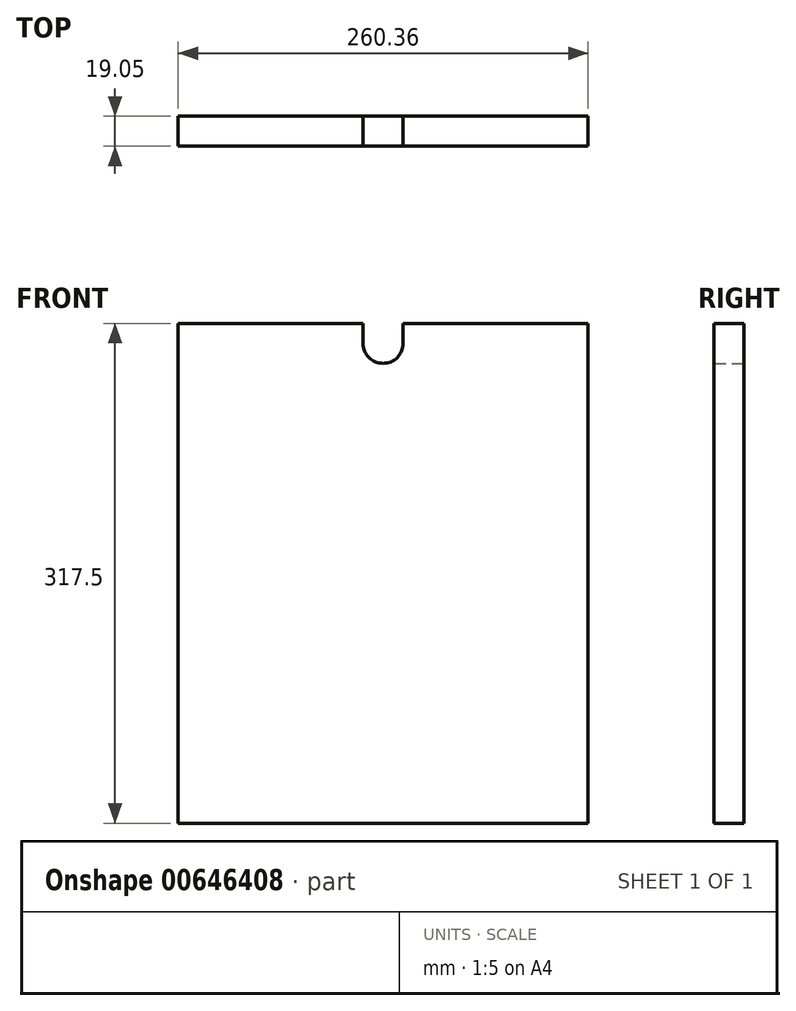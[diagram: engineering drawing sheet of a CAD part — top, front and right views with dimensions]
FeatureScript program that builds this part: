
annotation { "Feature Type Name" : "Feature", "Feature Type Description" : "" }
export const myFeature = defineFeature(function(context is Context, id is Id, definition is map)
    precondition{}
    {
        {
            var Q0;
            Q0=qCreatedBy(makeId("Front.planeOp"),FACE);
            var sketch = newSketch(context, id + "F0", { "sketchPlane" : qUnion([Q0])});
            skLineSegment(sketch, "E0.bottom", {"start": v(-130.18, 158.75) * mm, "end": v(130.18, 158.75) * mm});
            skLineSegment(sketch, "E0.top", {"start": v(-130.18, -158.75) * mm, "end": v(130.17, -158.75) * mm});
            skLineSegment(sketch, "E0.left", {"start": v(-130.17, 158.75) * mm, "end": v(-130.18, -158.75) * mm});
            skLineSegment(sketch, "E0.right", {"start": v(130.18, 158.75) * mm, "end": v(130.17, -158.75) * mm});
            skPoint(sketch, "E0.middle", {"position": v(0, 0) * mm});
            skLineSegment(sketch, "E1", {"start": v(0, 158.75) * mm, "end": v(0, 133.35) * mm});
            skPoint(sketch, "E1.endSnap0", {"position": v(0, 158.75) * mm});
            skCircle(sketch, "E2", {"center": v(0, 146.05) * mm, "radius": 12.7 * mm});
            skLineSegment(sketch, "E3", {"start": v(-12.7, 146.05) * mm, "end": v(-12.7, 158.75) * mm});
            skLineSegment(sketch, "E4", {"start": v(12.7, 146.05) * mm, "end": v(12.7, 158.75) * mm});
            skSolve(sketch);
        }
        {
            var Q0;
            Q0=makeQuery(id+"F0.imprint","IMPRINT",FACE,{"disambiguationData":[TD([[makeQuery(id+"F0.imprint","IMPRINT",EDGE,{"derivedFrom":sQuery(id+"F0.wireOp",EDGE,"E0.top")}),1.0]])]});
            extrude(context, id + "F1", {"entities" : qUnion([Q0]), "depth" : 19.05 * mm, "offsetDistance" : 25.4 * mm});
        }
    });
